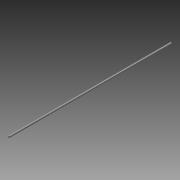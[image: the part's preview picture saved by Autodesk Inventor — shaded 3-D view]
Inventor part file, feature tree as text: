
AUTODESK INVENTOR PART (.ipt)
format: ipt  version: 2014 (Build 180170000, 170)  size: 67,584 bytes
history: native  units: in
note: dims shown in document units (in); Inventor stores cm internally (conversion verified against a paired STEP export)
features: extrude x1, sketch x1
ambient origin geometry x8: Origin, YZ Plane, XZ Plane, XY Plane, X Axis, Y Axis, Z Axis, Center Point
bodies: Solid1 (feature_tree)
feature tree (2):
  extrude  "Extrusion1"  Depth=0.25in
  sketch  "Sketch1"  dims[d0=32.5in d1=0.25in d2=0.25in d3=0.0in]
